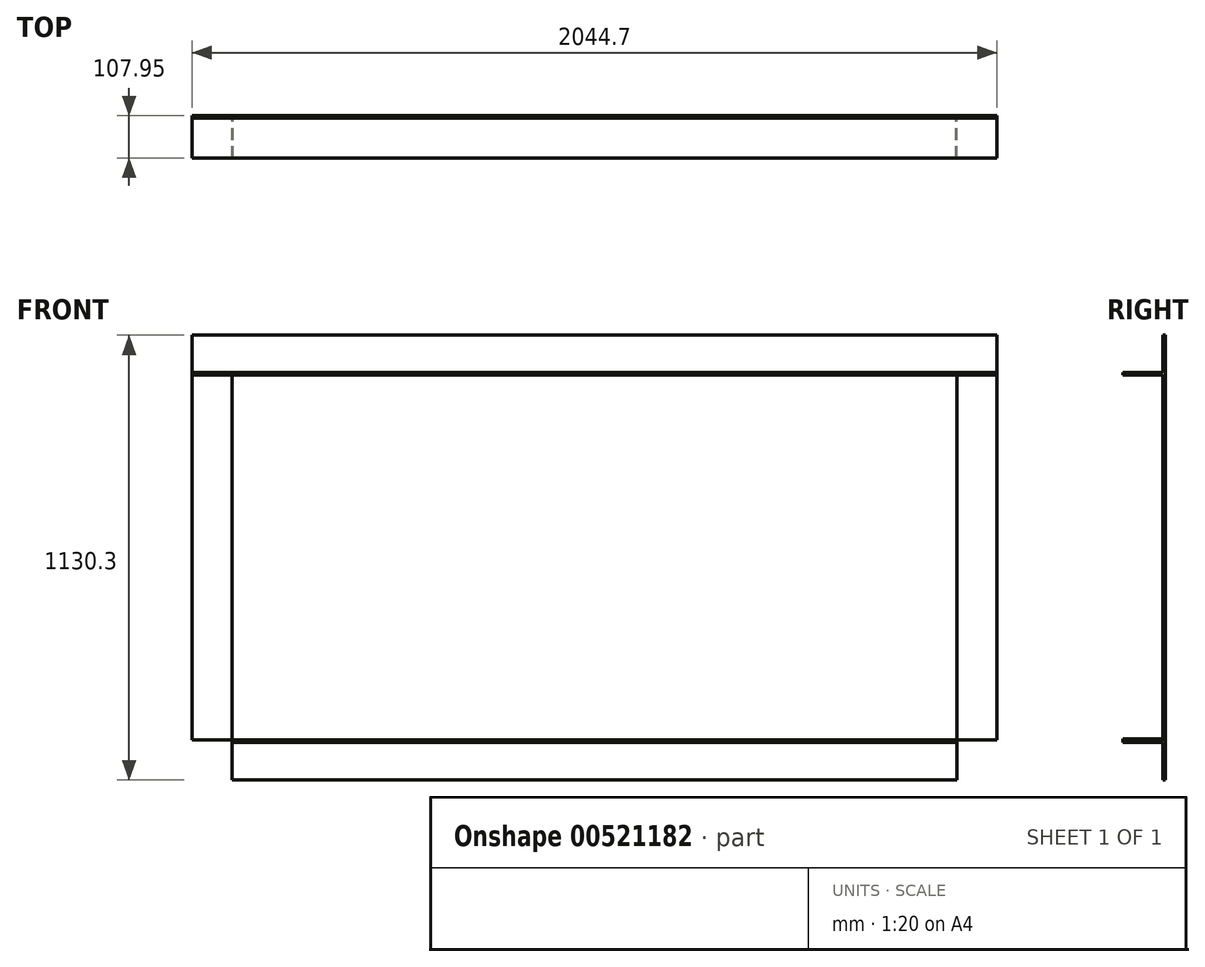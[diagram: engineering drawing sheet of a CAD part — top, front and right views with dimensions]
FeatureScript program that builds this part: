
annotation { "Feature Type Name" : "Feature", "Feature Type Description" : "" }
export const myFeature = defineFeature(function(context is Context, id is Id, definition is map)
    precondition{}
    {
        {
            var Q0;
            Q0=qCreatedBy(makeId("Front.planeOp"),FACE);
            var sketch = newSketch(context, id + "F0", { "sketchPlane" : qUnion([Q0])});
            skLineSegment(sketch, "E0.bottom", {"start": v(1885.72, 910.22) * mm, "end": v(44.22, 910.22) * mm});
            skLineSegment(sketch, "E0.left", {"start": v(1885.72, 910.22) * mm, "end": v(1885.72, -2.54) * mm});
            skLineSegment(sketch, "E0.right", {"start": v(44.22, 910.22) * mm, "end": v(44.22, -16.88) * mm});
            skLineSegment(sketch, "E1.bottom", {"start": v(44.22, 910.22) * mm, "end": v(-57.38, 910.22) * mm});
            skLineSegment(sketch, "E1.top", {"start": v(44.22, -16.88) * mm, "end": v(-57.38, -16.88) * mm});
            skLineSegment(sketch, "E1.right", {"start": v(-57.38, 910.22) * mm, "end": v(-57.38, -16.88) * mm});
            skLineSegment(sketch, "E2.bottom", {"start": v(1885.72, 910.22) * mm, "end": v(1987.32, 910.22) * mm});
            skLineSegment(sketch, "E2.top", {"start": v(1885.72, -16.88) * mm, "end": v(1987.32, -16.88) * mm});
            skLineSegment(sketch, "E2.left", {"start": v(1885.72, 910.22) * mm, "end": v(1885.72, -16.88) * mm});
            skLineSegment(sketch, "E2.right", {"start": v(1987.32, 910.22) * mm, "end": v(1987.32, -16.88) * mm});
            skLineSegment(sketch, "E3.bottom", {"start": v(44.22, -16.88) * mm, "end": v(1885.72, -16.88) * mm});
            skLineSegment(sketch, "E3.top", {"start": v(44.22, -118.48) * mm, "end": v(1885.72, -118.48) * mm});
            skLineSegment(sketch, "E3.left", {"start": v(44.22, -16.88) * mm, "end": v(44.22, -118.48) * mm});
            skLineSegment(sketch, "E3.right", {"start": v(1885.72, -16.88) * mm, "end": v(1885.72, -118.48) * mm});
            skLineSegment(sketch, "E4.bottom", {"start": v(-57.38, 910.22) * mm, "end": v(1987.32, 910.22) * mm});
            skLineSegment(sketch, "E4.top", {"start": v(-57.38, 1011.82) * mm, "end": v(1987.32, 1011.82) * mm});
            skLineSegment(sketch, "E4.left", {"start": v(-57.38, 910.22) * mm, "end": v(-57.38, 1011.82) * mm});
            skLineSegment(sketch, "E4.right", {"start": v(1987.32, 910.22) * mm, "end": v(1987.32, 1011.82) * mm});
            skLineSegment(sketch, "E5.left", {"start": v(1885.72, -2.54) * mm, "end": v(1885.72, 0) * mm});
            skLineSegment(sketch, "E6.bottom", {"start": v(44.22, -16.88) * mm, "end": v(46.76, -16.88) * mm});
            skLineSegment(sketch, "E6.top", {"start": v(44.22, -14.34) * mm, "end": v(46.76, -14.34) * mm});
            skLineSegment(sketch, "E6.left", {"start": v(44.22, -16.88) * mm, "end": v(44.22, -14.34) * mm});
            skLineSegment(sketch, "E6.right", {"start": v(46.76, -16.88) * mm, "end": v(46.76, -14.34) * mm});
            skLineSegment(sketch, "E7.bottom", {"start": v(1885.72, -16.88) * mm, "end": v(1883.18, -16.88) * mm});
            skLineSegment(sketch, "E7.top", {"start": v(1885.72, -14.34) * mm, "end": v(1883.18, -14.34) * mm});
            skLineSegment(sketch, "E7.left", {"start": v(1885.72, -16.88) * mm, "end": v(1885.72, -14.34) * mm});
            skLineSegment(sketch, "E7.right", {"start": v(1883.18, -16.88) * mm, "end": v(1883.18, -14.34) * mm});
            skSolve(sketch);
        }
        {
            var Q0;
            Q0=makeQuery(id+"F0.imprint","IMPRINT",FACE,{"disambiguationData":[TD([[makeQuery(id+"F0.imprint","IMPRINT",EDGE,{"derivedFrom":sQuery(id+"F0.wireOp",EDGE,"E7.bottom")}),-1.0]])]});
            var Q1;
            Q1=makeQuery(id+"F0.imprint","IMPRINT",FACE,{"disambiguationData":[TD([[makeQuery(id+"F0.imprint","IMPRINT",EDGE,{"derivedFrom":sQuery(id+"F0.wireOp",EDGE,"E2.top")}),1.0]])]});
            var Q2;
            Q2=makeQuery(id+"F0.imprint","IMPRINT",FACE,{"disambiguationData":[TD([[makeQuery(id+"F0.imprint","IMPRINT",EDGE,{"derivedFrom":sQuery(id+"F0.wireOp",EDGE,"E3.bottom")}),-1.0]])]});
            var Q3;
            Q3=makeQuery(id+"F0.imprint","IMPRINT",FACE,{"disambiguationData":[TD([[makeQuery(id+"F0.imprint","IMPRINT",EDGE,{"derivedFrom":sQuery(id+"F0.wireOp",EDGE,"E4.top")}),-1.0]])]});
            var Q4;
            Q4=makeQuery(id+"F0.imprint","IMPRINT",FACE,{"disambiguationData":[TD([[makeQuery(id+"F0.imprint","IMPRINT",EDGE,{"derivedFrom":sQuery(id+"F0.wireOp",EDGE,"E1.top")}),-1.0]])]});
            var Q5;
            Q5=makeQuery(id+"F0.imprint","IMPRINT",FACE,{"disambiguationData":[TD([[makeQuery(id+"F0.imprint","IMPRINT",EDGE,{"derivedFrom":sQuery(id+"F0.wireOp",EDGE,"E6.bottom")}),1.0]])]});
            extrude(context, id + "F1", {"entities" : qUnion([Q0, Q1, Q2, Q3, Q4, Q5]), "depth" : 6.35 * mm, "offsetDistance" : 25.4 * mm});
        }
        {
            var Q0;
            Q0=makeQuery(id+"F1.opExtrude","CAP_FACE",FACE,{"disambiguationData":[OSD([sQuery(id+"F0.wireOp",EDGE,"E1.top"),sQuery(id+"F0.wireOp",EDGE,"E0.right"),sQuery(id+"F0.wireOp",EDGE,"E1.right"),sQuery(id+"F0.wireOp",EDGE,"E2.top"),sQuery(id+"F0.wireOp",EDGE,"E2.left"),sQuery(id+"F0.wireOp",EDGE,"E2.right"),sQuery(id+"F0.wireOp",EDGE,"E3.bottom"),sQuery(id+"F0.wireOp",EDGE,"E3.top"),sQuery(id+"F0.wireOp",EDGE,"E3.left"),sQuery(id+"F0.wireOp",EDGE,"E3.right"),sQuery(id+"F0.wireOp",EDGE,"E4.bottom"),sQuery(id+"F0.wireOp",EDGE,"E4.top"),sQuery(id+"F0.wireOp",EDGE,"E4.left"),sQuery(id+"F0.wireOp",EDGE,"E4.right"),sQuery(id+"F0.wireOp",EDGE,"E5.left"),sQuery(id+"F0.wireOp",EDGE,"E6.top"),sQuery(id+"F0.wireOp",EDGE,"E6.right"),sQuery(id+"F0.wireOp",EDGE,"E7.top"),sQuery(id+"F0.wireOp",EDGE,"E7.right")])],"isStart":false});
            var sketch = newSketch(context, id + "F2", { "sketchPlane" : qUnion([Q0])});
            skLineSegment(sketch, "E8.0", {"start": v(44.22, 910.22) * mm, "end": v(1885.72, 910.22) * mm});
            skLineSegment(sketch, "E9.0", {"start": v(1987.32, 1011.82) * mm, "end": v(1987.32, -16.88) * mm});
            skLineSegment(sketch, "E10.0", {"start": v(1885.72, 910.22) * mm, "end": v(1885.72, -14.34) * mm});
            skLineSegment(sketch, "E11.0", {"start": v(-57.38, 1011.82) * mm, "end": v(1987.32, 1011.82) * mm});
            skLineSegment(sketch, "E12.0", {"start": v(-57.38, -16.88) * mm, "end": v(-57.38, 1011.82) * mm});
            skLineSegment(sketch, "E13.0", {"start": v(44.22, 910.22) * mm, "end": v(44.22, -14.34) * mm});
            skLineSegment(sketch, "E14.0", {"start": v(46.76, -16.88) * mm, "end": v(1883.18, -16.88) * mm});
            skLineSegment(sketch, "E15.0", {"start": v(44.22, -16.88) * mm, "end": v(44.22, -118.48) * mm});
            skLineSegment(sketch, "E16.0", {"start": v(1885.72, -16.88) * mm, "end": v(1885.72, -118.48) * mm});
            skLineSegment(sketch, "E17.0", {"start": v(44.22, -118.48) * mm, "end": v(1885.72, -118.48) * mm});
            skLineSegment(sketch, "E18.bottom", {"start": v(1987.32, 910.22) * mm, "end": v(-57.38, 910.22) * mm});
            skLineSegment(sketch, "E18.top", {"start": v(1987.32, 916.57) * mm, "end": v(-57.38, 916.57) * mm});
            skLineSegment(sketch, "E18.left", {"start": v(1987.32, 910.22) * mm, "end": v(1987.32, 916.57) * mm});
            skLineSegment(sketch, "E18.right", {"start": v(-57.38, 910.22) * mm, "end": v(-57.38, 916.57) * mm});
            skLineSegment(sketch, "E19.bottom", {"start": v(44.22, 910.22) * mm, "end": v(37.87, 910.22) * mm});
            skLineSegment(sketch, "E19.top", {"start": v(44.22, -16.88) * mm, "end": v(37.87, -16.88) * mm});
            skLineSegment(sketch, "E19.left", {"start": v(44.22, 910.22) * mm, "end": v(44.22, -16.88) * mm});
            skLineSegment(sketch, "E19.right", {"start": v(37.87, 910.22) * mm, "end": v(37.87, -16.88) * mm});
            skLineSegment(sketch, "E20.bottom", {"start": v(1885.72, 910.22) * mm, "end": v(1892.07, 910.22) * mm});
            skLineSegment(sketch, "E20.top", {"start": v(1885.72, -16.88) * mm, "end": v(1892.07, -16.88) * mm});
            skLineSegment(sketch, "E20.left", {"start": v(1885.72, 910.22) * mm, "end": v(1885.72, -16.88) * mm});
            skLineSegment(sketch, "E20.right", {"start": v(1892.07, 910.22) * mm, "end": v(1892.07, -16.88) * mm});
            skLineSegment(sketch, "E21.bottom", {"start": v(1885.72, -16.88) * mm, "end": v(44.22, -16.88) * mm});
            skLineSegment(sketch, "E21.top", {"start": v(1885.72, -23.23) * mm, "end": v(44.22, -23.23) * mm});
            skLineSegment(sketch, "E21.left", {"start": v(1885.72, -16.88) * mm, "end": v(1885.72, -23.23) * mm});
            skLineSegment(sketch, "E21.right", {"start": v(44.22, -16.88) * mm, "end": v(44.22, -23.23) * mm});
            skLineSegment(sketch, "E22.0", {"start": v(44.22, -14.34) * mm, "end": v(46.76, -14.34) * mm});
            skLineSegment(sketch, "E23.0", {"start": v(46.76, -16.88) * mm, "end": v(46.76, -14.34) * mm});
            skLineSegment(sketch, "E24.0", {"start": v(1885.72, -14.34) * mm, "end": v(1883.18, -14.34) * mm});
            skLineSegment(sketch, "E25.0", {"start": v(1883.18, -16.88) * mm, "end": v(1883.18, -14.34) * mm});
            skSolve(sketch);
        }
        {
            var Q0;
            Q0=makeQuery(id+"F2.imprint","IMPRINT",FACE,{"disambiguationData":[TD([[makeQuery(id+"F2.imprint","IMPRINT",EDGE,{"derivedFrom":sQuery(id+"F2.wireOp",EDGE,"E18.top")}),1.0]])]});
            var Q1;
            {var subQ3=sQuery(id+"F2.wireOp",EDGE,"E20.bottom");Q1=makeQuery(id+"F2.imprint","IMPRINT",FACE,{"disambiguationData":[TD([[makeQuery(id+"F2.imprint","IMPRINT",EDGE,{"derivedFrom":subQ3}),-1.0]])]});}
            var Q2;
            {var subQ3=sQuery(id+"F2.wireOp",EDGE,"E19.bottom");Q2=makeQuery(id+"F2.imprint","IMPRINT",FACE,{"disambiguationData":[TD([[makeQuery(id+"F2.imprint","IMPRINT",EDGE,{"derivedFrom":subQ3}),1.0]])]});}
            var Q3;
            Q3=makeQuery(id+"F2.imprint","IMPRINT",FACE,{"disambiguationData":[TD([[makeQuery(id+"F2.imprint","IMPRINT",EDGE,{"derivedFrom":sQuery(id+"F2.wireOp",EDGE,"E21.top")}),-1.0]])]});
            var Q4;
            {var subQ3=sQuery(id+"F2.wireOp",EDGE,"E22.0");Q4=makeQuery(id+"F2.imprint","IMPRINT",FACE,{"disambiguationData":[TD([[makeQuery(id+"F2.imprint","IMPRINT",EDGE,{"derivedFrom":subQ3}),-1.0]])]});}
            var Q5;
            {var subQ3=sQuery(id+"F2.wireOp",EDGE,"E24.0");Q5=makeQuery(id+"F2.imprint","IMPRINT",FACE,{"disambiguationData":[TD([[makeQuery(id+"F2.imprint","IMPRINT",EDGE,{"derivedFrom":subQ3}),1.0]])]});}
            extrude(context, id + "F3", {"entities" : qUnion([Q0, Q1, Q2, Q3, Q4, Q5]), "operationType" : NewBodyOperationType.ADD, "depth" : 101.6 * mm, "offsetDistance" : 25.4 * mm});
        }
    });
